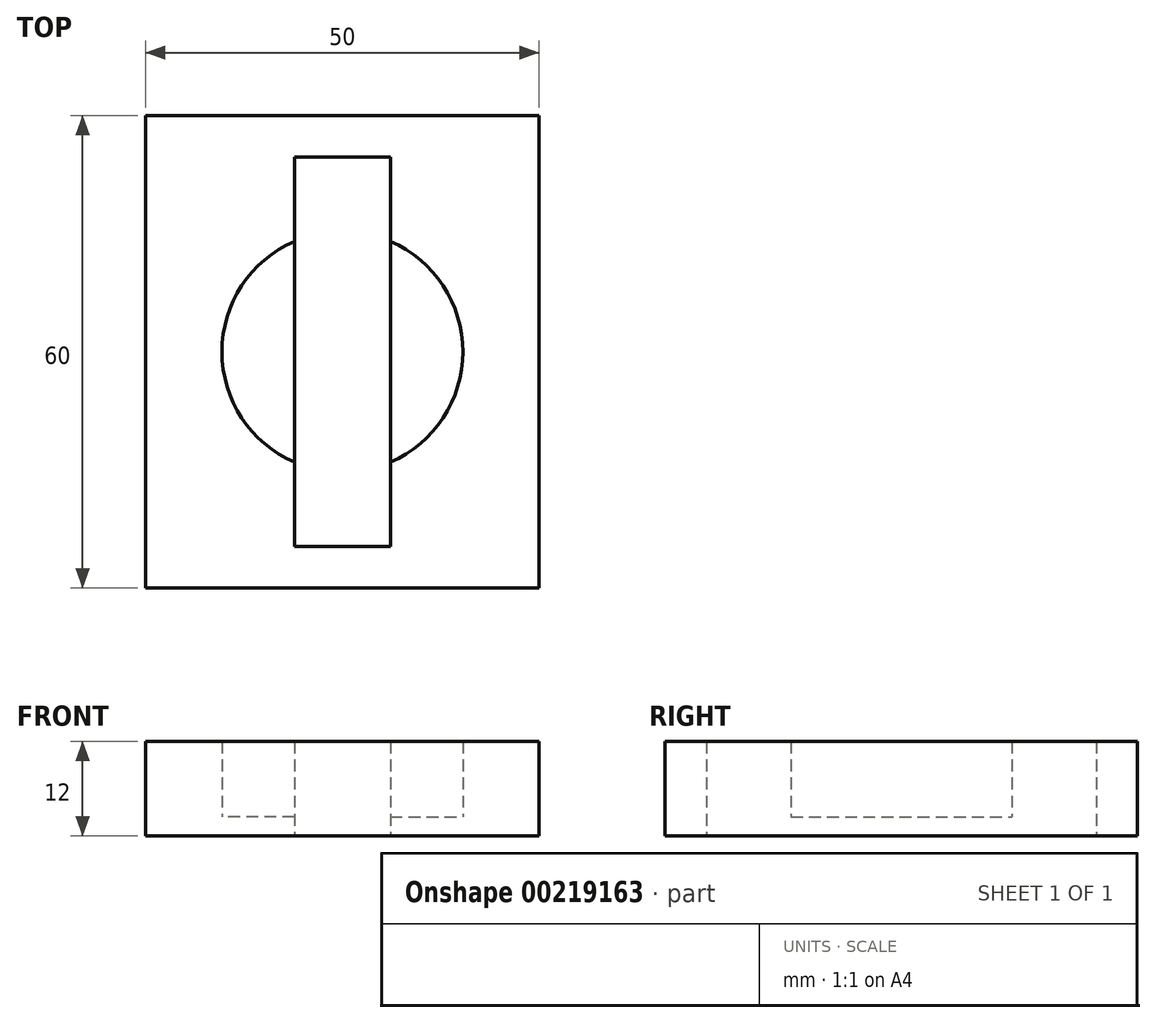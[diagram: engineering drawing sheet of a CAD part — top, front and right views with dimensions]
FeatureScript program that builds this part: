
annotation { "Feature Type Name" : "Feature", "Feature Type Description" : "" }
export const myFeature = defineFeature(function(context is Context, id is Id, definition is map)
    precondition{}
    {
        {
            var Q0;
            Q0=qCreatedBy(makeId("Top.planeOp"),FACE);
            var sketch = newSketch(context, id + "F0", { "sketchPlane" : qUnion([Q0])});
            skLineSegment(sketch, "E0.bottom", {"start": v(6.1, -24.75) * mm, "end": v(-6.1, -24.75) * mm});
            skLineSegment(sketch, "E0.top", {"start": v(6.1, 24.75) * mm, "end": v(-6.1, 24.75) * mm});
            skLineSegment(sketch, "E0.left", {"start": v(6.1, -24.75) * mm, "end": v(6.1, 24.75) * mm});
            skLineSegment(sketch, "E0.right", {"start": v(-6.1, -24.75) * mm, "end": v(-6.1, 24.75) * mm});
            skPoint(sketch, "E0.middle", {"position": v(0, 0) * mm});
            skLineSegment(sketch, "E1.bottom", {"start": v(25, -30) * mm, "end": v(-25, -30) * mm});
            skLineSegment(sketch, "E1.top", {"start": v(25, 30) * mm, "end": v(-25, 30) * mm});
            skLineSegment(sketch, "E1.left", {"start": v(25, -30) * mm, "end": v(25, 30) * mm});
            skLineSegment(sketch, "E1.right", {"start": v(-25, -30) * mm, "end": v(-25, 30) * mm});
            skCircle(sketch, "E2", {"center": v(0, 0) * mm, "radius": 15.3 * mm});
            skSolve(sketch);
        }
        {
            var Q0;
            {var subQ4=sQuery(id+"F0.wireOp",EDGE,"E0.bottom");Q0=makeQuery(id+"F0.imprint","IMPRINT",FACE,{"disambiguationData":[TD([[makeQuery(id+"F0.imprint","IMPRINT",EDGE,{"derivedFrom":subQ4}),1.0]])]});}
            extrude(context, id + "F1", {"entities" : qUnion([Q0]), "depth" : 12 * mm});
        }
        {
            var Q0;
            {var subQ0=sQuery(id+"F0.wireOp",EDGE,"E2");var subQ1=sQuery(id+"F0.wireOp",EDGE,"E0.right");var subQ2=makeQuery(id+"F0.imprint","INTERSECT",VERTEX,{"disambiguationData":[OD(0.0)],"derivedFrom":[subQ1,subQ0]});Q0=makeQuery(id+"F0.imprint","IMPRINT",FACE,{"disambiguationData":[TD([[makeQuery(id+"F0.imprint","IMPRINT",EDGE,{"disambiguationData":[TD([[subQ2,-1.0]])],"derivedFrom":subQ1}),1.0]])]});}
            var Q1;
            {var subQ0=sQuery(id+"F0.wireOp",EDGE,"E2");var subQ1=sQuery(id+"F0.wireOp",EDGE,"E0.left");var subQ2=makeQuery(id+"F0.imprint","INTERSECT",VERTEX,{"disambiguationData":[OD(0.0)],"derivedFrom":[subQ1,subQ0]});Q1=makeQuery(id+"F0.imprint","IMPRINT",FACE,{"disambiguationData":[TD([[makeQuery(id+"F0.imprint","IMPRINT",EDGE,{"disambiguationData":[TD([[subQ2,-1.0]])],"derivedFrom":subQ1}),-1.0]])]});}
            extrude(context, id + "F2", {"entities" : qUnion([Q0, Q1]), "operationType" : NewBodyOperationType.ADD, "depth" : 2.4 * mm});
        }
    });
